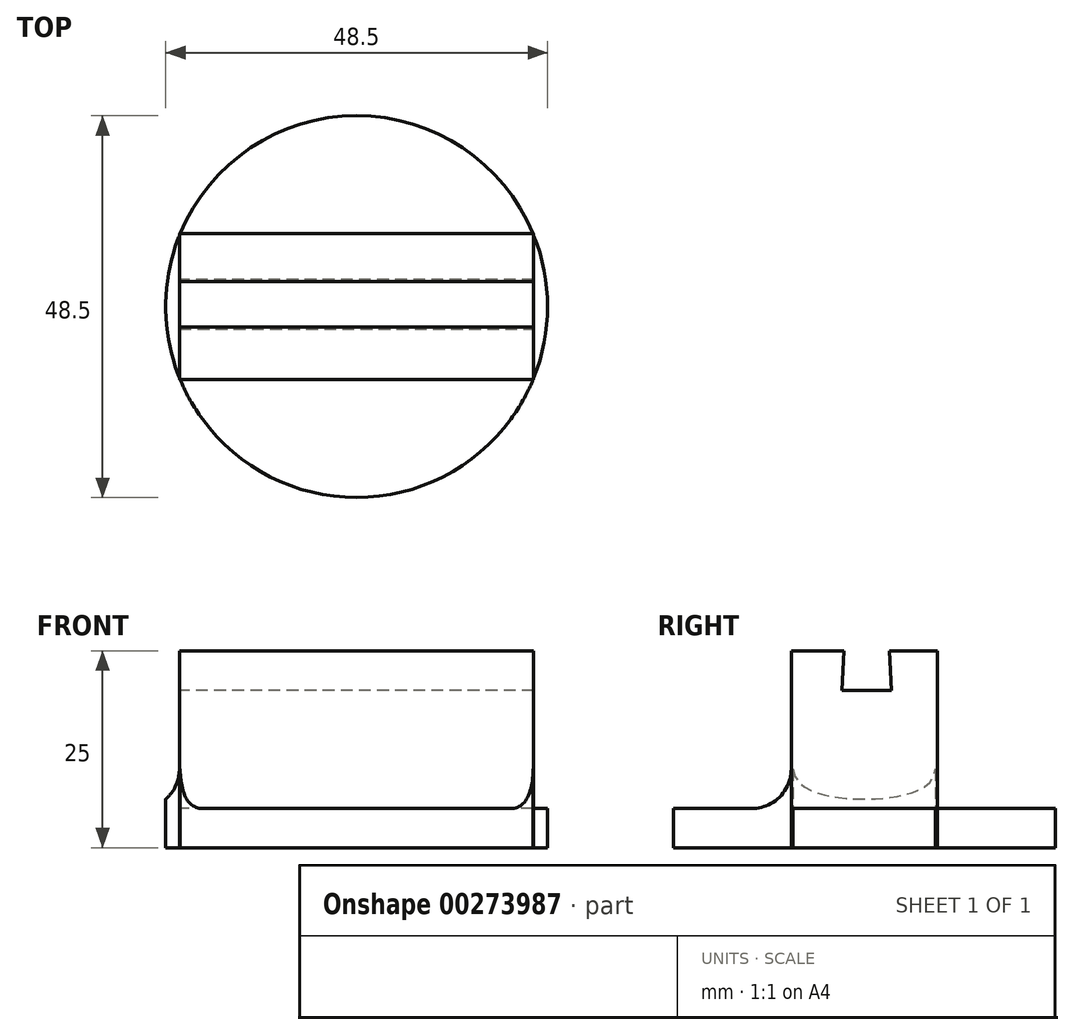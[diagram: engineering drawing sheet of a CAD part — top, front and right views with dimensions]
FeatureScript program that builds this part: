
annotation { "Feature Type Name" : "Feature", "Feature Type Description" : "" }
export const myFeature = defineFeature(function(context is Context, id is Id, definition is map)
    precondition{}
    {
        {
            var Q0;
            Q0=qCreatedBy(makeId("Top.planeOp"),FACE);
            var sketch = newSketch(context, id + "F0", { "sketchPlane" : qUnion([Q0])});
            skCircle(sketch, "E0", {"center": v(0, 0) * mm, "radius": 24.25 * mm});
            skSolve(sketch);
        }
        {
            var Q0;
            Q0=makeQuery(id+"F0.imprint","IMPRINT",FACE,{"disambiguationData":[TD([[makeQuery(id+"F0.imprint","IMPRINT",EDGE,{"derivedFrom":sQuery(id+"F0.wireOp",EDGE,"E0")}),1.0]])]});
            extrude(context, id + "F1", {"entities" : qUnion([Q0]), "depth" : 5 * mm});
        }
        {
            var Q0;
            Q0=qCreatedBy(makeId("Top.planeOp"),FACE);
            var sketch = newSketch(context, id + "F2", { "sketchPlane" : qUnion([Q0])});
            skLineSegment(sketch, "E1.bottom", {"start": v(-22.5, 9.3) * mm, "end": v(22.5, 9.3) * mm});
            skLineSegment(sketch, "E1.top", {"start": v(-22.5, -9.3) * mm, "end": v(22.5, -9.3) * mm});
            skLineSegment(sketch, "E1.left", {"start": v(-22.5, 9.3) * mm, "end": v(-22.5, -9.3) * mm});
            skLineSegment(sketch, "E1.right", {"start": v(22.5, 9.3) * mm, "end": v(22.5, -9.3) * mm});
            skSolve(sketch);
        }
        {
            var Q0;
            Q0 = qSketchRegion(id + "F2", true);
            extrude(context, id + "F3", {"entities" : qUnion([Q0]), "operationType" : NewBodyOperationType.ADD, "depth" : 25 * mm});
        }
        {
            var Q0;
            Q0=makeQuery(id+"F3.opExtrude","CAP_FACE",FACE,{"disambiguationData":[OSD([sQuery(id+"F2.wireOp",EDGE,"E1.bottom"),sQuery(id+"F2.wireOp",EDGE,"E1.top"),sQuery(id+"F2.wireOp",EDGE,"E1.left"),sQuery(id+"F2.wireOp",EDGE,"E1.right")])],"isStart":false});
            var sketch = newSketch(context, id + "F4", { "sketchPlane" : qUnion([Q0])});
            skLineSegment(sketch, "E2.bottom", {"start": v(-22.5, 3.2) * mm, "end": v(22.5, 3.2) * mm});
            skLineSegment(sketch, "E2.top", {"start": v(-22.5, -2.59) * mm, "end": v(22.5, -2.59) * mm});
            skLineSegment(sketch, "E2.left", {"start": v(-22.5, 3.2) * mm, "end": v(-22.5, -2.59) * mm});
            skLineSegment(sketch, "E2.right", {"start": v(22.5, 3.2) * mm, "end": v(22.5, -2.59) * mm});
            skSolve(sketch);
        }
        {
            var Q0;
            Q0 = qSketchRegion(id + "F4", true);
            extrude(context, id + "F5", {"entities" : qUnion([Q0]), "operationType" : NewBodyOperationType.ADD, "oppositeDirection" : true, "depth" : 5 * mm});
        }
        {
            var Q0;
            Q0 = qSketchRegion(id + "F4", true);
            extrude(context, id + "F6", {"entities" : qUnion([Q0]), "operationType" : NewBodyOperationType.ADD, "oppositeDirection" : true, "depth" : 5 * mm, "hasDraft" : true, "draftAngle" : 3 * degree});
        }
        {
            var Q0;
            Q0 = qSketchRegion(id + "F4", true);
            extrude(context, id + "F7", {"entities" : qUnion([Q0]), "operationType" : NewBodyOperationType.REMOVE, "oppositeDirection" : true, "depth" : 5 * mm, "hasDraft" : true, "draftAngle" : 3 * degree});
        }
        {
            var Q0;
            Q0=makeQuery(id+"F3.boolean.opBoolean","INTERSECT",EDGE,{"derivedFrom":[makeQuery(id+"F1.opExtrude","CAP_FACE",FACE,{"disambiguationData":[OSD([sQuery(id+"F0.wireOp",EDGE,"E0")])],"isStart":false}),makeQuery(id+"F3.opExtrude","SWEPT_FACE",FACE,{"disambiguationData":[OSD([sQuery(id+"F2.wireOp",EDGE,"E1.top")])]})]});
            fillet(context, id + "F8", {"entities" : qUnion([Q0]), "radius" : 5 * mm, "tangentPropagation" : true, "allowEdgeOverflow" : false});
        }
        {
            var Q0;
            Q0=makeQuery(id+"F3.boolean.opBoolean","INTERSECT",EDGE,{"derivedFrom":[makeQuery(id+"F1.opExtrude","CAP_FACE",FACE,{"disambiguationData":[OSD([sQuery(id+"F0.wireOp",EDGE,"E0")])],"isStart":false}),makeQuery(id+"F3.opExtrude","SWEPT_FACE",FACE,{"disambiguationData":[OSD([sQuery(id+"F2.wireOp",EDGE,"E1.left")])]})]});
            fillet(context, id + "F9", {"entities" : qUnion([Q0]), "radius" : 5 * mm, "tangentPropagation" : true, "allowEdgeOverflow" : false});
        }
    });
